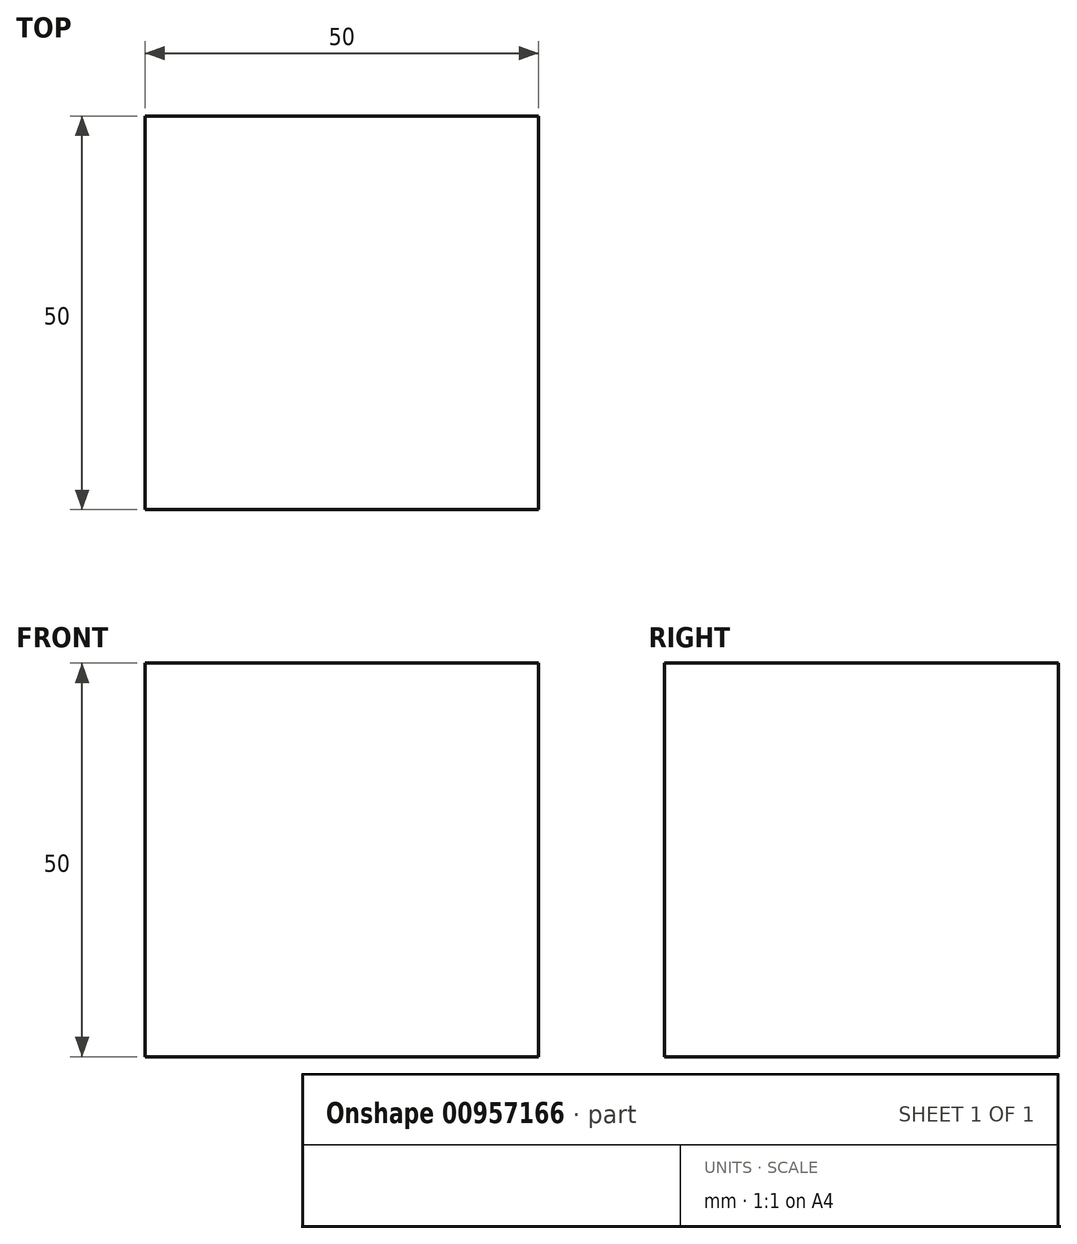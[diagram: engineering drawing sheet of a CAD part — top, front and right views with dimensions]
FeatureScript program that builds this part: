
annotation { "Feature Type Name" : "Feature", "Feature Type Description" : "" }
export const myFeature = defineFeature(function(context is Context, id is Id, definition is map)
    precondition{}
    {
        {
            var Q0;
            Q0=qCreatedBy(makeId("Front.planeOp"),FACE);
            var sketch = newSketch(context, id + "F0", { "sketchPlane" : qUnion([Q0])});
            skLineSegment(sketch, "E0", {"start": v(0, 0) * mm, "end": v(0, 50) * mm});
            skLineSegment(sketch, "E1", {"start": v(0, 50) * mm, "end": v(50, 50) * mm});
            skLineSegment(sketch, "E2", {"start": v(50, 50) * mm, "end": v(50, 0) * mm});
            skLineSegment(sketch, "E3", {"start": v(50, 0) * mm, "end": v(0, 0) * mm});
            skSolve(sketch);
        }
        {
            var Q0;
            Q0=makeQuery(id+"F0.imprint","IMPRINT",FACE,{"disambiguationData":[TD([[makeQuery(id+"F0.imprint","IMPRINT",EDGE,{"derivedFrom":sQuery(id+"F0.wireOp",EDGE,"E0")}),-1.0]])]});
            extrude(context, id + "F1", {"entities" : qUnion([Q0]), "depth" : 50 * mm, "offsetDistance" : 25 * mm});
        }
    });
